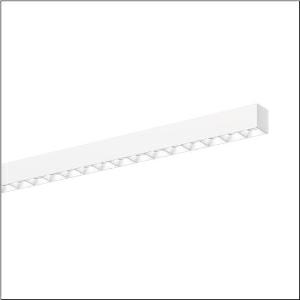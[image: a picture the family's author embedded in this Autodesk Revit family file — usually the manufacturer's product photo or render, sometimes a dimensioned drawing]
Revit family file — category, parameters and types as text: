
# Revit family: silica_r__21_51mx26db45wb_cce2
name_source: partatom
category: Lighting Fixtures
units: mm (PartAtom-declared; Revit-internal decimal feet)

## family parameters
Cut with Voids When Loaded = No
Host = Face
Light Source = No
Part Type = Normal
Room Calculation Point = No
Round Connector Dimension = Use Diameter
Shared = No

## types (1)
- --- (1 x LED, 5400 lm, 29.3 W, 4000K)
    Apparent Load = 29 VA
    CIE Flux Codes = 83 98 100 100 100
    Color Rendering = 80
    Color Temperature = 4000K
    Default Elevation = 1800 mm
    Description = Silica® 21, office luminaire, primary light control with darklight reflector, of PMMA, white, CAT 2 (L<= 3000cd/m²), light emission: direct distribution, primary light characteristic: symmetric, installation type: surface-mounted, LED, rated luminous flux: 5.400lm, luminous efficacy: 184lm/W, light colour: 840, colour temperature: 4000K, with terminal, 3+2-pole, max. 2.5mm², mains connection: 220..240V, AC, 50/60Hz, rated input power: 29.3W, luminaire housing, of aluminium, traffic white (RAL 9016), length: 1.504mm, width: 53mm, height: 53mm, protection rating (complete): IP20, insulation class (complete): insulation class I (protective earthing), certification: CE, permissible operating ambient temperature: 0..+35°C, standard: EN 50419, packaging unit: 1 piece
    Height = 0 mm  [stored 0 ft]
    Lamp = 1 x LED
    Lamp Light Flux = 5400 lm
    Lamp Power = 29.3 W
    Lamp count = 1
    Length = 1504 mm
    Luminous efficacy = 184 lm/W
    Manufacturer = Siteco
    ModVariant = No
    Model = 51MX26DB45WB
    Mounting Place = Ceiling
    Mounting Type = Recessed
    Number of Poles = 1
    OnlyDefault = Yes
    Power Factor = 1
    Product Name = Silica® 21
    Product group = office luminaire | ceiling recessed
    ProductGroupID = 401
    Protection Class = Protection class I
    Protection Degree = IP 20
    RLX_Detail_Level = 1
    RLX_Emergency_Light_Flux = 0 lm
    RLX_Emergency_Type = 0
    RLX_Emergency_Type_DB = No
    RlxData = <blob elided: 41957 chars, md5=3543779d>
    Socket = socket
    Standby Power = 0 W
    System Light Flux = 5400 lm
    System Power = 29 W
    Type Comments = factory setting: luminous flux: 100 % | dim-lin: 254 | 336 mA
    Type Image = l_1297772.jpg
    URL = http://relux.com
    VarID = @adj_055409
    Voltage = 0 V
    Weight = 0.00 kg
    Width = 53 mm

note: [stored X ft] marks values corroborated as IEEE doubles in the binary element streams (Revit-internal decimal feet)

## geometry (parser evidence)
native form markers: Blend x4, Sweep x11
no freeform markers — native parametric forms only
